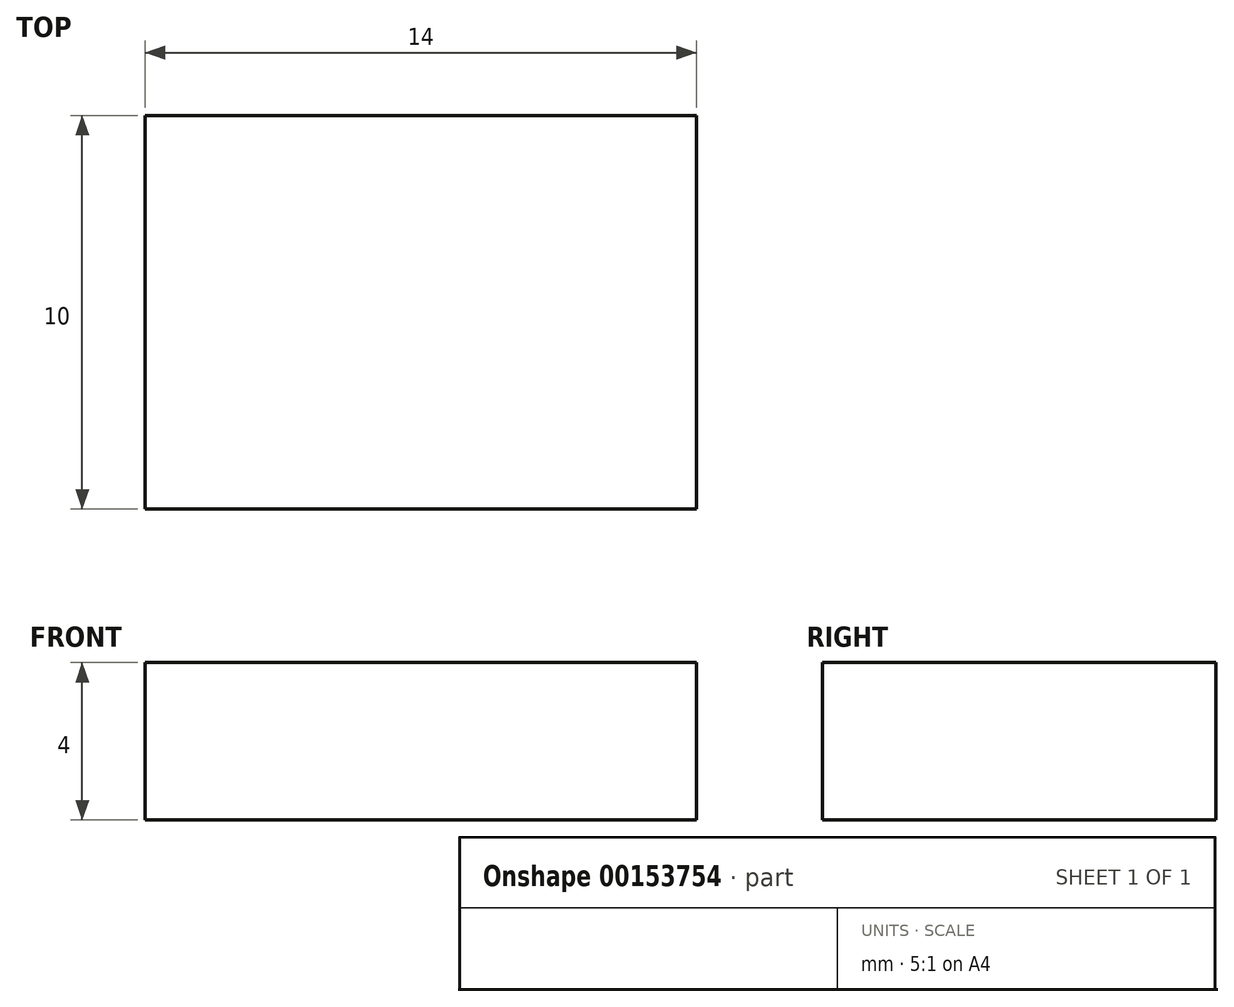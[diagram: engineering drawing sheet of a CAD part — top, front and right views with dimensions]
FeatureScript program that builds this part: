
annotation { "Feature Type Name" : "Feature", "Feature Type Description" : "" }
export const myFeature = defineFeature(function(context is Context, id is Id, definition is map)
    precondition{}
    {
        {
            var Q0;
            Q0=qCreatedBy(makeId("Right.planeOp"),FACE);
            var sketch = newSketch(context, id + "F0", { "sketchPlane" : qUnion([Q0])});
            skLineSegment(sketch, "E0.left", {"start": v(0, 0) * mm, "end": v(0, 0) * mm});
            skLineSegment(sketch, "E0.right", {"start": v(-3.66, 0) * mm, "end": v(-3.66, 0) * mm});
            skLineSegment(sketch, "E1.bottom", {"start": v(-5, 2) * mm, "end": v(5, 2) * mm});
            skLineSegment(sketch, "E1.top", {"start": v(-5, -2) * mm, "end": v(5, -2) * mm});
            skLineSegment(sketch, "E1.left", {"start": v(-5, 2) * mm, "end": v(-5, -2) * mm});
            skLineSegment(sketch, "E1.right", {"start": v(5, 2) * mm, "end": v(5, -2) * mm});
            skPoint(sketch, "E1.middle", {"position": v(0, 0) * mm});
            skSolve(sketch);
        }
        {
            var Q0;
            Q0=makeQuery(id+"F0.imprint","IMPRINT",FACE,{"disambiguationData":[TD([[makeQuery(id+"F0.imprint","IMPRINT",EDGE,{"derivedFrom":sQuery(id+"F0.wireOp",EDGE,"E1.bottom")}),-1.0]])]});
            extrude(context, id + "F1", {"entities" : qUnion([Q0]), "oppositeDirection" : true, "depth" : 14 * mm});
        }
    });
